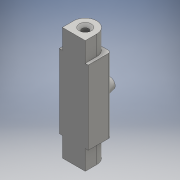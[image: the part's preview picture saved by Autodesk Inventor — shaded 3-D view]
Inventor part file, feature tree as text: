
AUTODESK INVENTOR PART (.ipt)
format: ipt  version: 2016 (Build 200138000, 138)  size: 187,392 bytes
history: native  units: mm
features: extrude x6, sketch x6, fillet x2, chamfer x1
ambient origin geometry x8: Origin, YZ Plane, XZ Plane, XY Plane, X Axis, Y Axis, Z Axis, Center Point
bodies: Solid1 (feature_tree)
feature tree (15):
  extrude  "Extrusion1"  Depth=8.5mm TaperAngle=0.0deg
  extrude  "Extrusion2"  Depth=4.25mm
  extrude  "Extrusion3"  Depth=8.5mm TaperAngle=0.0deg
  extrude  "Extrusion4"  Depth=7.3mm TaperAngle=0.0deg
  extrude  "Extrusion5"  Depth=4.0mm
  extrude  "Extrusion6"  Depth=1.0mm
  fillet  "Fillet1"  Radius=19.0mm
  fillet  "Fillet2"  Radius=3.5mm
  chamfer  "Chamfer1"  Distance=1.0mm
  sketch  "Sketch1"  dims[d1=42.0mm d2=8.5mm d3=0.0mm]
  sketch  "Sketch2"  dims[d4=2.5mm d5=4.25mm]
  sketch  "Sketch3"  dims[d6=5.35mm d7=8.5mm d8=0.0mm]
  sketch  "Sketch4"  dims[d10=7.3mm d11=0.0mm d13=7.3mm d14=0.0mm]
  sketch  "Sketch5"  dims[d19=4.0mm d20=4.0mm]
  sketch  "Sketch6"  dims[d21=8.7mm d22=1.0mm d23=19.0mm d24=3.5mm d25=0.0mm d26=1.0mm d27=1.0mm d28=3.0mm d29=0.0mm d30=2.0mm d31=1.0mm d32=1.0mm d33=2.0mm d34=45.0deg d35=4.25mm d36=4.25mm d37=4.25mm]
